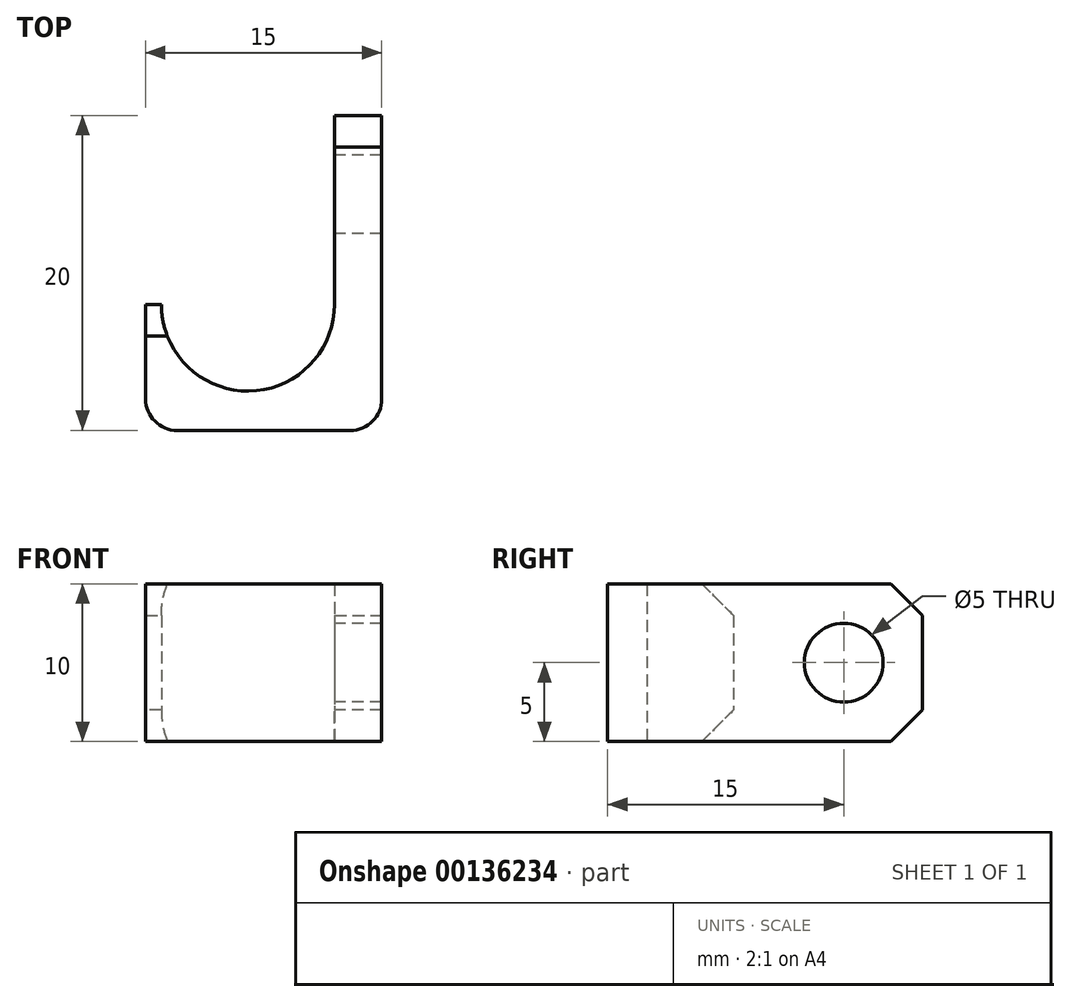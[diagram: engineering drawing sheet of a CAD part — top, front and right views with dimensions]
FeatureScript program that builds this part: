
annotation { "Feature Type Name" : "Feature", "Feature Type Description" : "" }
export const myFeature = defineFeature(function(context is Context, id is Id, definition is map)
    precondition{}
    {
        {
            var Q0;
            Q0=qCreatedBy(makeId("Top.planeOp"),FACE);
            var sketch = newSketch(context, id + "F0", { "sketchPlane" : qUnion([Q0])});
            skLineSegment(sketch, "E0", {"start": v(0, 2) * mm, "end": v(0, 20) * mm});
            skLineSegment(sketch, "E1", {"start": v(0, 20) * mm, "end": v(-3, 20) * mm});
            skLineSegment(sketch, "E2", {"start": v(-3, 20) * mm, "end": v(-3, 8) * mm});
            skLineSegment(sketch, "E3", {"start": v(-15, 8) * mm, "end": v(-15, 2) * mm});
            skLineSegment(sketch, "E4", {"start": v(-13, 0) * mm, "end": v(-2, 0) * mm});
            skArc(sketch, "E5", {"start": v(-14, 8) * mm, "mid": v(-8.5, 2.5) * mm, "end": v(-3, 8) * mm});
            skLineSegment(sketch, "E6.trimOffspring", {"start": v(-14, 8) * mm, "end": v(-15, 8) * mm});
            skPoint(sketch, "E7.visualSharp", {"position": v(0, 0) * mm});
            skArc(sketch, "E7.filletArc", {"start": v(-2, 0) * mm, "mid": v(-0.59, 0.59) * mm, "end": v(0, 2) * mm});
            skPoint(sketch, "E8.visualSharp", {"position": v(-15, 0) * mm});
            skArc(sketch, "E8.filletArc", {"start": v(-15, 2) * mm, "mid": v(-14.41, 0.59) * mm, "end": v(-13, 0) * mm});
            skSolve(sketch);
        }
        {
            var Q0;
            Q0=makeQuery(id+"F0.imprint","IMPRINT",FACE,{"disambiguationData":[TD([[makeQuery(id+"F0.imprint","IMPRINT",EDGE,{"derivedFrom":sQuery(id+"F0.wireOp",EDGE,"E0")}),1.0]])]});
            extrude(context, id + "F1", {"entities" : qUnion([Q0]), "depth" : 10 * mm});
        }
        {
            var Q0;
            Q0=makeQuery(id+"F1.opExtrude","CAP_EDGE",EDGE,{"disambiguationData":[OSD([sQuery(id+"F0.wireOp",EDGE,"E6.trimOffspring")])],"isStart":false});
            var Q1;
            Q1=makeQuery(id+"F1.opExtrude","CAP_EDGE",EDGE,{"disambiguationData":[OSD([sQuery(id+"F0.wireOp",EDGE,"E6.trimOffspring")])],"isStart":true});
            var Q2;
            Q2=makeQuery(id+"F1.opExtrude","CAP_EDGE",EDGE,{"disambiguationData":[OSD([sQuery(id+"F0.wireOp",EDGE,"E1")])],"isStart":true});
            var Q3;
            Q3=makeQuery(id+"F1.opExtrude","CAP_EDGE",EDGE,{"disambiguationData":[OSD([sQuery(id+"F0.wireOp",EDGE,"E1")])],"isStart":false});
            chamfer(context, id + "F2", {"entities" : qUnion([Q0, Q1, Q2, Q3]), "width" : 2 * mm, "tangentPropagation" : true});
        }
        {
            var Q0;
            Q0=makeQuery(id+"F1.opExtrude","SWEPT_FACE",FACE,{"disambiguationData":[OSD([sQuery(id+"F0.wireOp",EDGE,"E2")])]});
            var sketch = newSketch(context, id + "F3", { "sketchPlane" : qUnion([Q0])});
            skCircle(sketch, "E9", {"center": v(-15, 5) * mm, "radius": 2.5 * mm});
            skSolve(sketch);
        }
        {
            var Q0;
            Q0=makeQuery(id+"F3.imprint","IMPRINT",FACE,{"disambiguationData":[TD([[makeQuery(id+"F3.imprint","IMPRINT",EDGE,{"derivedFrom":sQuery(id+"F3.wireOp",EDGE,"E9")}),1.0]])]});
            extrude(context, id + "F4", {"entities" : qUnion([Q0]), "operationType" : NewBodyOperationType.REMOVE, "oppositeDirection" : true, "depth" : 25 * mm});
        }
    });
